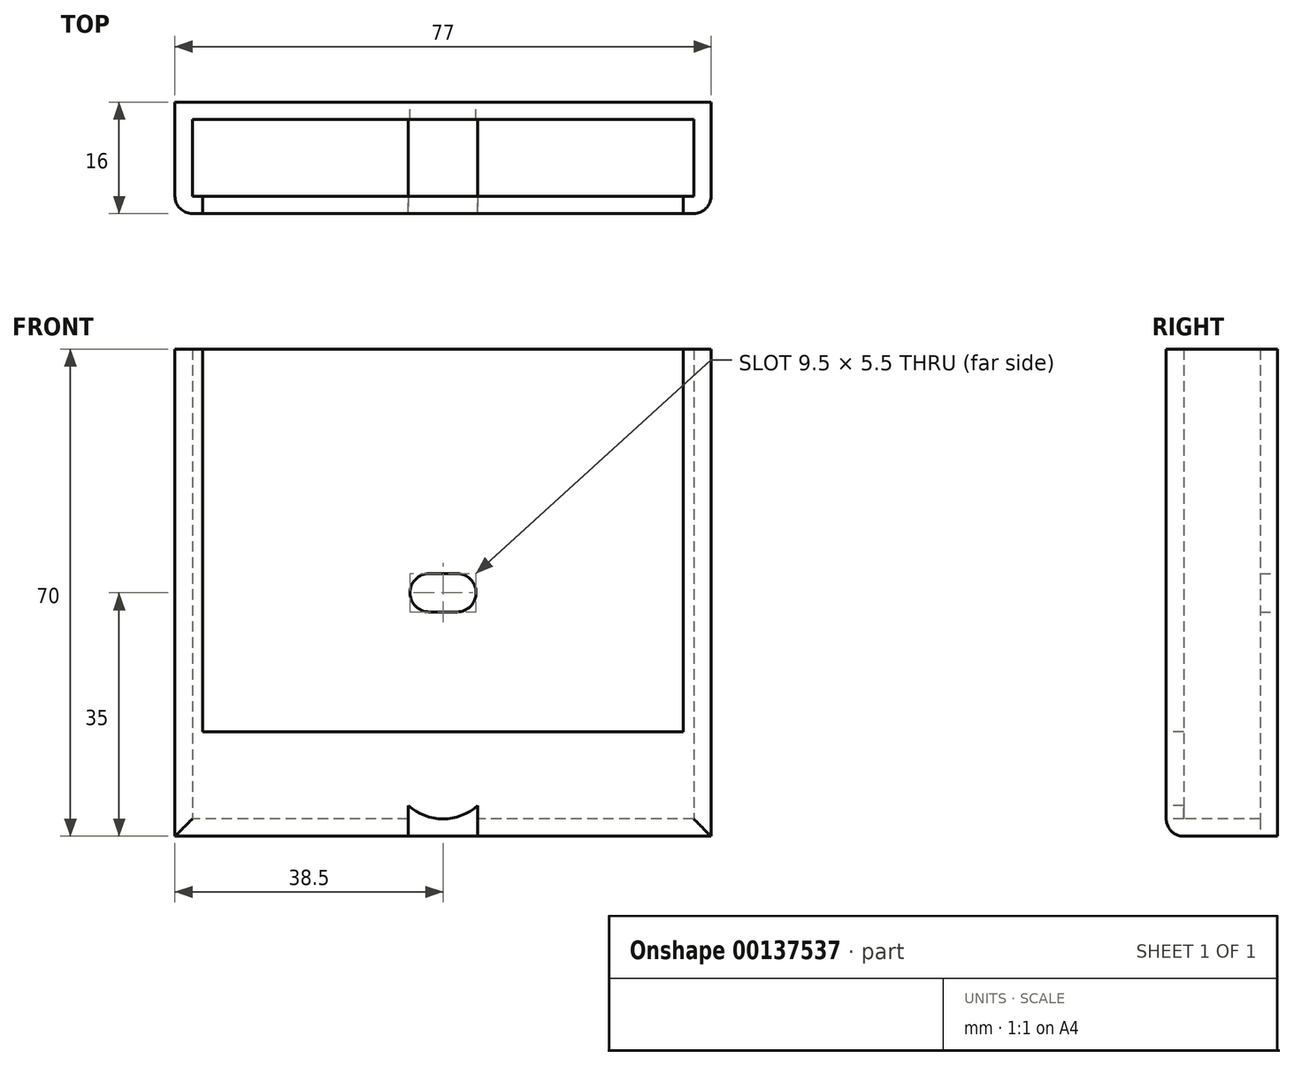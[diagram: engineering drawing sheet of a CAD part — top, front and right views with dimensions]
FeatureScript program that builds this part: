
annotation { "Feature Type Name" : "Feature", "Feature Type Description" : "" }
export const myFeature = defineFeature(function(context is Context, id is Id, definition is map)
    precondition{}
    {
        {
            var Q0;
            Q0=qCreatedBy(makeId("Front.planeOp"),FACE);
            var sketch = newSketch(context, id + "F0", { "sketchPlane" : qUnion([Q0])});
            skLineSegment(sketch, "E0.bottom", {"start": v(38.5, 35) * mm, "end": v(-38.5, 35) * mm});
            skLineSegment(sketch, "E0.top", {"start": v(38.5, -35) * mm, "end": v(-38.5, -35) * mm});
            skLineSegment(sketch, "E0.left", {"start": v(38.5, 35) * mm, "end": v(38.5, -35) * mm});
            skLineSegment(sketch, "E0.right", {"start": v(-38.5, 35) * mm, "end": v(-38.5, -35) * mm});
            skPoint(sketch, "E0.middle", {"position": v(0, 0) * mm});
            skSolve(sketch);
        }
        {
            var Q0;
            Q0 = qSketchRegion(id + "F0", true);
            extrude(context, id + "F1", {"entities" : qUnion([Q0]), "endBound" : BoundingType.SYMMETRIC, "depth" : 16 * mm});
        }
        {
            var Q0;
            Q0=makeQuery(id+"F1.opExtrude","SWEPT_FACE",FACE,{"disambiguationData":[OSD([sQuery(id+"F0.wireOp",EDGE,"E0.bottom")])]});
            shell(context, id + "F2", {"entities" : qUnion([Q0]), "thickness" : 2.5 * mm});
        }
        {
            var Q0;
            Q0=makeQuery(id+"F1.opExtrude","CAP_FACE",FACE,{"disambiguationData":[OSD([sQuery(id+"F0.wireOp",EDGE,"E0.bottom"),sQuery(id+"F0.wireOp",EDGE,"E0.top"),sQuery(id+"F0.wireOp",EDGE,"E0.left"),sQuery(id+"F0.wireOp",EDGE,"E0.right")])],"isStart":false});
            var sketch = newSketch(context, id + "F3", { "sketchPlane" : qUnion([Q0])});
            skLineSegment(sketch, "E1.bottom", {"start": v(-34.5, 35) * mm, "end": v(34.5, 35) * mm});
            skLineSegment(sketch, "E1.top", {"start": v(-34.5, -20) * mm, "end": v(34.5, -20) * mm});
            skLineSegment(sketch, "E1.left", {"start": v(-34.5, 35) * mm, "end": v(-34.5, -20) * mm});
            skLineSegment(sketch, "E1.right", {"start": v(34.5, 35) * mm, "end": v(34.5, -20) * mm});
            skLineSegment(sketch, "E2", {"start": v(0, 0) * mm, "end": v(0, -35) * mm, "construction": true});
            skLineSegment(sketch, "E3.bottom", {"start": v(-7.5, -20) * mm, "end": v(7.5, -20) * mm});
            skLineSegment(sketch, "E3.left", {"start": v(-7.5, -20) * mm, "end": v(-7.5, -25) * mm});
            skLineSegment(sketch, "E3.right", {"start": v(7.5, -20) * mm, "end": v(7.5, -25) * mm});
            skArc(sketch, "E4", {"start": v(-7.5, -25) * mm, "mid": v(0, -32.5) * mm, "end": v(7.5, -25) * mm});
            skLineSegment(sketch, "E5.bottom", {"start": v(-5, -35) * mm, "end": v(5, -35) * mm});
            skLineSegment(sketch, "E5.left", {"start": v(-5, -35) * mm, "end": v(-5, -30.6) * mm});
            skLineSegment(sketch, "E5.right", {"start": v(5, -35) * mm, "end": v(5, -30.6) * mm});
            skSolve(sketch);
        }
        {
            var Q0;
            Q0=makeQuery(id+"F3.imprint","IMPRINT",FACE,{"disambiguationData":[TD([[makeQuery(id+"F3.imprint","IMPRINT",EDGE,{"derivedFrom":sQuery(id+"F3.wireOp",EDGE,"E1.bottom")}),1.0]])]});
            var Q1;
            Q1=makeQuery(id+"F3.imprint","IMPRINT",FACE,{"disambiguationData":[TD([[makeQuery(id+"F3.imprint","IMPRINT",EDGE,{"derivedFrom":sQuery(id+"F3.wireOp",EDGE,"E3.bottom")}),-1.0]])]});
            var Q2;
            Q2=makeQuery(id+"F3.imprint","IMPRINT",FACE,{"disambiguationData":[TD([[makeQuery(id+"F3.imprint","IMPRINT",EDGE,{"derivedFrom":sQuery(id+"F3.wireOp",EDGE,"E5.bottom")}),-1.0]])]});
            var Q3;
            {var subQ0=sQuery(id+"F0.wireOp",EDGE,"E0.right");var subQ1=sQuery(id+"F0.wireOp",EDGE,"E0.left");var subQ2=sQuery(id+"F0.wireOp",EDGE,"E0.top");var subQ3=sQuery(id+"F0.wireOp",EDGE,"E0.bottom");Q3=makeQuery(id+"F2.opShell","OFFSET_FACE",FACE,{"disambiguationData":[OSD([subQ3,subQ2,subQ1,subQ0]),TDD([makeQuery(id+"F1.opExtrude","CAP_FACE",FACE,{"disambiguationData":[OSD([subQ3,subQ2,subQ1,subQ0])],"isStart":true})])]});}
            extrude(context, id + "F4", {"entities" : qUnion([Q0, Q1, Q2]), "operationType" : NewBodyOperationType.REMOVE, "endBound" : BoundingType.UP_TO_SURFACE, "oppositeDirection" : true, "endBoundEntityFace" : qUnion([Q3]), "depth" : 25 * mm});
        }
        {
            var Q0;
            Q0=makeQuery(id+"F1.opExtrude","CAP_FACE",FACE,{"disambiguationData":[OSD([sQuery(id+"F0.wireOp",EDGE,"E0.bottom"),sQuery(id+"F0.wireOp",EDGE,"E0.top"),sQuery(id+"F0.wireOp",EDGE,"E0.left"),sQuery(id+"F0.wireOp",EDGE,"E0.right")])],"isStart":true});
            var sketch = newSketch(context, id + "F5", { "sketchPlane" : qUnion([Q0])});
            skLineSegment(sketch, "E6.bottom", {"start": v(2, 2.75) * mm, "end": v(-2, 2.75) * mm});
            skLineSegment(sketch, "E6.top", {"start": v(2, -2.75) * mm, "end": v(-2, -2.75) * mm});
            skPoint(sketch, "E6.middle", {"position": v(0, 0) * mm});
            skArc(sketch, "E7", {"start": v(2, 2.75) * mm, "mid": v(4.75, 0) * mm, "end": v(2, -2.75) * mm});
            skArc(sketch, "E8.MirrorCS", {"start": v(-2, 2.75) * mm, "mid": v(-4.75, 0) * mm, "end": v(-2, -2.75) * mm});
            skSolve(sketch);
        }
        {
            var Q0;
            Q0=makeQuery(id+"F5.imprint","IMPRINT",FACE,{"disambiguationData":[TD([[makeQuery(id+"F5.imprint","IMPRINT",EDGE,{"derivedFrom":sQuery(id+"F5.wireOp",EDGE,"E6.bottom")}),1.0]])]});
            extrude(context, id + "F6", {"entities" : qUnion([Q0]), "operationType" : NewBodyOperationType.REMOVE, "endBound" : BoundingType.UP_TO_NEXT, "oppositeDirection" : true, "depth" : 25 * mm});
        }
        {
            var Q0;
            Q0=makeQuery(id+"F1.opExtrude","CAP_EDGE",EDGE,{"disambiguationData":[OSD([sQuery(id+"F0.wireOp",EDGE,"E0.left")])],"isStart":false});
            var Q1;
            Q1=makeQuery(id+"F1.opExtrude","CAP_EDGE",EDGE,{"disambiguationData":[OSD([sQuery(id+"F0.wireOp",EDGE,"E0.right")])],"isStart":false});
            var Q2;
            {var subQ0=sQuery(id+"F0.wireOp",EDGE,"E0.right");var subQ1=sQuery(id+"F0.wireOp",EDGE,"E0.top");Q2=makeQuery(id+"F4.boolean.opBoolean","SPLIT",EDGE,{"disambiguationData":[TD([makeQuery(id+"F1.opExtrude","SWEPT_FACE",FACE,{"disambiguationData":[OSD([subQ0])]})])],"derivedFrom":makeQuery(id+"F1.opExtrude","CAP_EDGE",EDGE,{"disambiguationData":[OSD([subQ1])],"isStart":false})});}
            var Q3;
            {var subQ0=sQuery(id+"F0.wireOp",EDGE,"E0.left");var subQ1=sQuery(id+"F0.wireOp",EDGE,"E0.top");Q3=makeQuery(id+"F4.boolean.opBoolean","SPLIT",EDGE,{"disambiguationData":[TD([makeQuery(id+"F1.opExtrude","SWEPT_FACE",FACE,{"disambiguationData":[OSD([subQ0])]})])],"derivedFrom":makeQuery(id+"F1.opExtrude","CAP_EDGE",EDGE,{"disambiguationData":[OSD([subQ1])],"isStart":false})});}
            var Q4;
            {var subQ0=sQuery(id+"F3.wireOp",EDGE,"E4");Q4=makeQuery(id+"F4.boolean.opBoolean","COPY",EDGE,{"derivedFrom":makeQuery(id+"F4.opExtrude","CAP_EDGE",EDGE,{"disambiguationData":[OSD([subQ0]),TDD([makeQuery(id+"F3.imprint","IMPRINT",EDGE,{"disambiguationData":[TD([[makeQuery(id+"F3.imprint","INTERSECT",VERTEX,{"derivedFrom":[sQuery(id+"F3.wireOp",EDGE,"E3.left"),subQ0]}),-1.0]])],"derivedFrom":subQ0})])],"isStart":true})});}
            var Q5;
            {var subQ0=sQuery(id+"F3.wireOp",EDGE,"E4");Q5=makeQuery(id+"F4.boolean.opBoolean","COPY",EDGE,{"derivedFrom":makeQuery(id+"F4.opExtrude","CAP_EDGE",EDGE,{"disambiguationData":[OSD([subQ0]),TDD([makeQuery(id+"F3.imprint","IMPRINT",EDGE,{"disambiguationData":[TD([[makeQuery(id+"F3.imprint","INTERSECT",VERTEX,{"derivedFrom":[sQuery(id+"F3.wireOp",EDGE,"E3.right"),subQ0]}),1.0]])],"derivedFrom":subQ0})])],"isStart":true})});}
            var Q6;
            {var subQ0=sQuery(id+"F3.wireOp",EDGE,"E1.top");Q6=makeQuery(id+"F4.boolean.opBoolean","COPY",EDGE,{"derivedFrom":makeQuery(id+"F4.opExtrude","CAP_EDGE",EDGE,{"disambiguationData":[OSD([subQ0]),TDD([makeQuery(id+"F3.imprint","IMPRINT",EDGE,{"disambiguationData":[TD([[makeQuery(id+"F3.imprint","INTERSECT",VERTEX,{"derivedFrom":[subQ0,sQuery(id+"F3.wireOp",EDGE,"E1.right")]}),1.0]])],"derivedFrom":subQ0})])],"isStart":true})});}
            var Q7;
            {var subQ0=sQuery(id+"F3.wireOp",EDGE,"E1.top");Q7=makeQuery(id+"F4.boolean.opBoolean","COPY",EDGE,{"derivedFrom":makeQuery(id+"F4.opExtrude","CAP_EDGE",EDGE,{"disambiguationData":[OSD([subQ0]),TDD([makeQuery(id+"F3.imprint","IMPRINT",EDGE,{"disambiguationData":[TD([[makeQuery(id+"F3.imprint","INTERSECT",VERTEX,{"derivedFrom":[subQ0,sQuery(id+"F3.wireOp",EDGE,"E1.left")]}),-1.0]])],"derivedFrom":subQ0})])],"isStart":true})});}
            var Q8;
            Q8=makeQuery(id+"F4.boolean.opBoolean","COPY",EDGE,{"derivedFrom":makeQuery(id+"F4.opExtrude","CAP_EDGE",EDGE,{"disambiguationData":[OSD([sQuery(id+"F3.wireOp",EDGE,"E1.right")])],"isStart":true})});
            var Q9;
            Q9=makeQuery(id+"F4.boolean.opBoolean","COPY",EDGE,{"derivedFrom":makeQuery(id+"F4.opExtrude","CAP_EDGE",EDGE,{"disambiguationData":[OSD([sQuery(id+"F3.wireOp",EDGE,"E1.left")])],"isStart":true})});
            fillet(context, id + "F7", {"entities" : qUnion([Q0, Q1, Q2, Q3, Q4, Q5, Q6, Q7, Q8, Q9]), "radius" : 2.5 * mm, "tangentPropagation" : true, "allowEdgeOverflow" : false});
        }
    });
